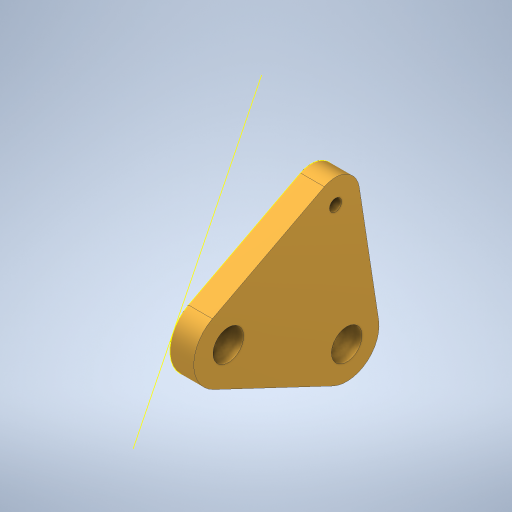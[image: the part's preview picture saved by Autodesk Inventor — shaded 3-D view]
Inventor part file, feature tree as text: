
AUTODESK INVENTOR PART (.ipt)
format: ipt  version: 2023 (Build 270158000, 158)  size: 258,560 bytes
history: native  units: in
note: dims shown in document units (in); Inventor stores cm internally (conversion verified against a paired STEP export)
features: other x3, sketch x1
ambient origin geometry x8: Origin, YZ Plane, XZ Plane, XY Plane, X Axis, Y Axis, Z Axis, Center Point
bodies: Solid1 (feature_tree)
feature tree (4):
  other  "Kauri modular camera mount mini.ipt"
  other  "Solid1::Kauri modular camera mount mini.ipt"
  other  "TaggingFeature1"
  sketch  "Sketch2"  dims[d0=0.3937in]
